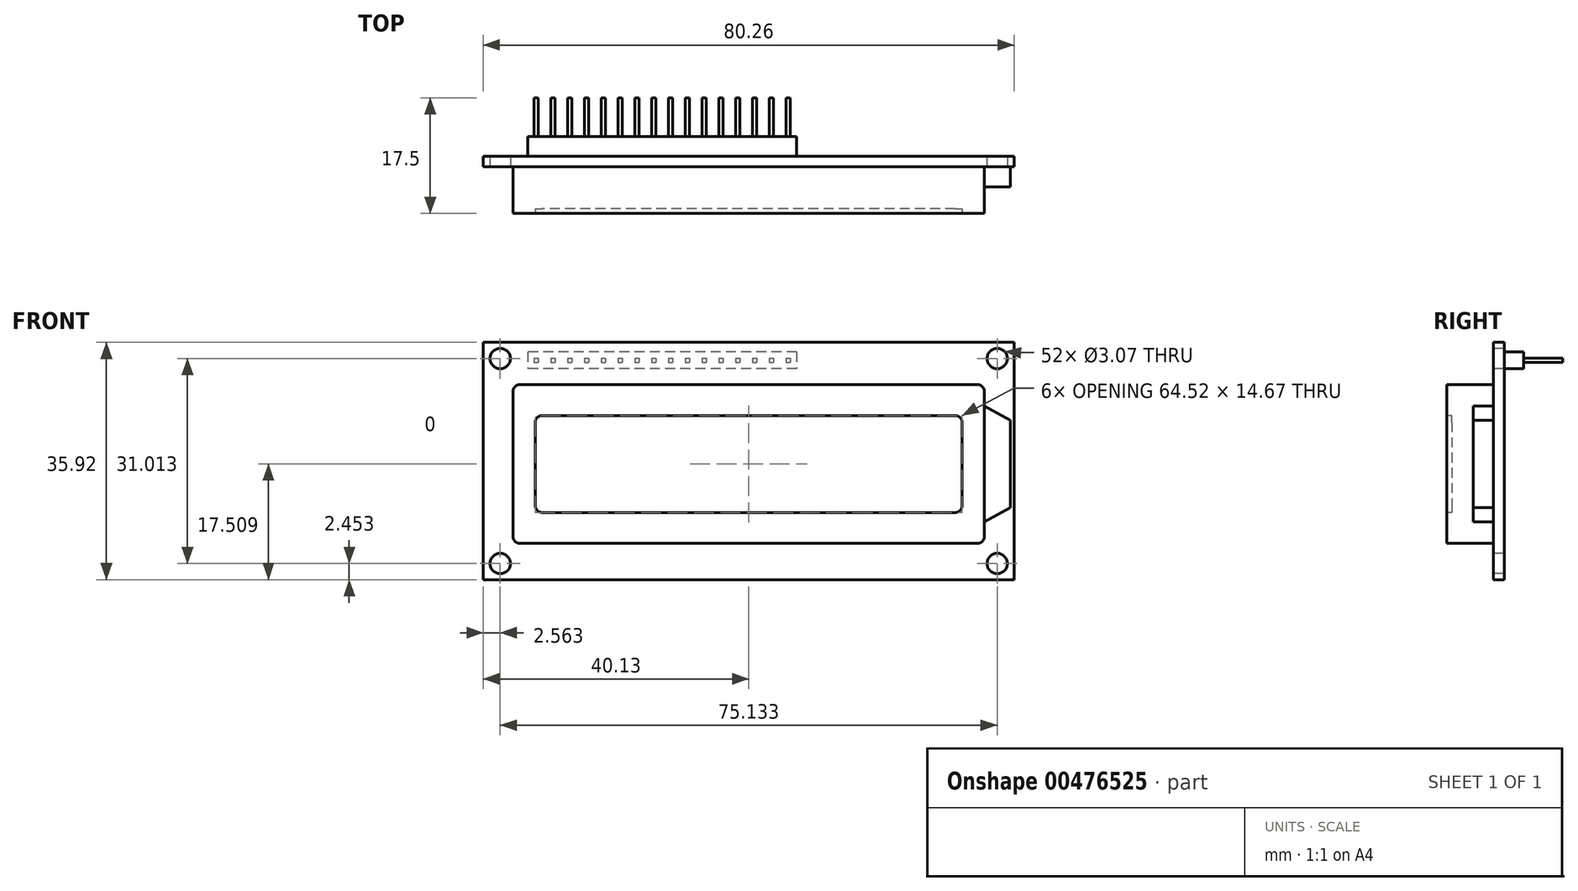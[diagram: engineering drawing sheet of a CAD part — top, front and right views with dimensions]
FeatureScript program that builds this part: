
annotation { "Feature Type Name" : "Feature", "Feature Type Description" : "" }
export const myFeature = defineFeature(function(context is Context, id is Id, definition is map)
    precondition{}
    {
        {
            var Q0;
            Q0=qCreatedBy(makeId("Front.planeOp"),FACE);
            var sketch = newSketch(context, id + "F0", { "sketchPlane" : qUnion([Q0])});
            skLineSegment(sketch, "E0.bottom", {"start": v(40.13, 17.96) * mm, "end": v(-40.13, 17.96) * mm});
            skLineSegment(sketch, "E0.top", {"start": v(40.13, -17.96) * mm, "end": v(-40.13, -17.96) * mm});
            skLineSegment(sketch, "E0.left", {"start": v(40.13, 17.96) * mm, "end": v(40.13, -17.96) * mm});
            skLineSegment(sketch, "E0.right", {"start": v(-40.13, 17.96) * mm, "end": v(-40.13, -17.96) * mm});
            skPoint(sketch, "E0.middle", {"position": v(0, 0) * mm});
            skCircle(sketch, "E1", {"center": v(-37.57, -15.5) * mm, "radius": 1.54 * mm});
            skLineSegment(sketch, "E2", {"start": v(0, 0) * mm, "end": v(0, 12.09) * mm, "construction": true});
            skLineSegment(sketch, "E3", {"start": v(0, 0) * mm, "end": v(12.95, 0) * mm, "construction": true});
            skCircle(sketch, "E4.MirrorC", {"center": v(-37.57, 15.5) * mm, "radius": 1.54 * mm});
            skCircle(sketch, "E5.MirrorC", {"center": v(37.57, -15.5) * mm, "radius": 1.54 * mm});
            skCircle(sketch, "E6.MirrorC", {"center": v(37.57, 15.5) * mm, "radius": 1.54 * mm});
            skSolve(sketch);
        }
        {
            var Q0;
            Q0 = qSketchRegion(id + "F0", true);
            extrude(context, id + "F1", {"entities" : qUnion([Q0]), "oppositeDirection" : true, "depth" : 1.6 * mm});
        }
        {
            var Q0;
            Q0=makeQuery(id+"F1.opExtrude","CAP_FACE",FACE,{"disambiguationData":[OSD([sQuery(id+"F0.wireOp",EDGE,"E0.bottom"),sQuery(id+"F0.wireOp",EDGE,"E0.top"),sQuery(id+"F0.wireOp",EDGE,"E0.left"),sQuery(id+"F0.wireOp",EDGE,"E0.right"),sQuery(id+"F0.wireOp",EDGE,"E4.MirrorC"),sQuery(id+"F0.wireOp",EDGE,"E1"),sQuery(id+"F0.wireOp",EDGE,"E5.MirrorC"),sQuery(id+"F0.wireOp",EDGE,"E6.MirrorC")])],"isStart":true});
            var sketch = newSketch(context, id + "F2", { "sketchPlane" : qUnion([Q0])});
            skLineSegment(sketch, "E7.bottom", {"start": v(-34.6, -12.46) * mm, "end": v(34.6, -12.46) * mm});
            skLineSegment(sketch, "E7.top", {"start": v(-34.6, 11.56) * mm, "end": v(34.6, 11.56) * mm});
            skLineSegment(sketch, "E7.left", {"start": v(-35.62, -11.44) * mm, "end": v(-35.62, 10.54) * mm});
            skLineSegment(sketch, "E7.right", {"start": v(35.62, -11.44) * mm, "end": v(35.62, 10.54) * mm});
            skLineSegment(sketch, "E8", {"start": v(0, 0) * mm, "end": v(0, -12.46) * mm, "construction": true});
            skPoint(sketch, "E8.endSnap0", {"position": v(0, -12.46) * mm});
            skPoint(sketch, "E9.visualSharp", {"position": v(-35.62, 11.56) * mm});
            skArc(sketch, "E9.filletArc", {"start": v(-34.6, 11.56) * mm, "mid": v(-35.33, 11.26) * mm, "end": v(-35.62, 10.54) * mm});
            skPoint(sketch, "E10.visualSharp", {"position": v(-35.62, -12.46) * mm});
            skArc(sketch, "E10.filletArc", {"start": v(-35.62, -11.44) * mm, "mid": v(-35.33, -12.16) * mm, "end": v(-34.6, -12.46) * mm});
            skPoint(sketch, "E11.visualSharp", {"position": v(35.62, -12.46) * mm});
            skArc(sketch, "E11.filletArc", {"start": v(34.6, -12.46) * mm, "mid": v(35.33, -12.16) * mm, "end": v(35.62, -11.44) * mm});
            skPoint(sketch, "E12.visualSharp", {"position": v(35.62, 11.56) * mm});
            skArc(sketch, "E12.filletArc", {"start": v(35.62, 10.54) * mm, "mid": v(35.33, 11.26) * mm, "end": v(34.6, 11.56) * mm});
            skSolve(sketch);
        }
        {
            var Q0;
            Q0=makeQuery(id+"F2.imprint","IMPRINT",FACE,{"disambiguationData":[TD([[makeQuery(id+"F2.imprint","IMPRINT",EDGE,{"derivedFrom":sQuery(id+"F2.wireOp",EDGE,"E7.bottom")}),1.0]])]});
            extrude(context, id + "F3", {"entities" : qUnion([Q0]), "depth" : 7.06 * mm});
        }
        {
            var Q0;
            Q0=makeQuery(id+"F3.opExtrude","CAP_FACE",FACE,{"disambiguationData":[OSD([sQuery(id+"F2.wireOp",EDGE,"E7.bottom"),sQuery(id+"F2.wireOp",EDGE,"E7.top"),sQuery(id+"F2.wireOp",EDGE,"E7.left"),sQuery(id+"F2.wireOp",EDGE,"E7.right"),sQuery(id+"F2.wireOp",EDGE,"E9.filletArc"),sQuery(id+"F2.wireOp",EDGE,"E10.filletArc"),sQuery(id+"F2.wireOp",EDGE,"E11.filletArc"),sQuery(id+"F2.wireOp",EDGE,"E12.filletArc")])],"isStart":false});
            var sketch = newSketch(context, id + "F4", { "sketchPlane" : qUnion([Q0])});
            skLineSegment(sketch, "E13.bottom", {"start": v(31.24, 6.88) * mm, "end": v(-31.24, 6.88) * mm});
            skLineSegment(sketch, "E13.top", {"start": v(31.24, -7.79) * mm, "end": v(-31.24, -7.79) * mm});
            skLineSegment(sketch, "E13.left", {"start": v(32.26, 5.87) * mm, "end": v(32.26, -6.77) * mm});
            skLineSegment(sketch, "E13.right", {"start": v(-32.26, 5.87) * mm, "end": v(-32.26, -6.77) * mm});
            skPoint(sketch, "E13.middle", {"position": v(0, -0.45) * mm});
            skLineSegment(sketch, "E14", {"start": v(-34.6, -11.44) * mm, "end": v(34.6, 10.54) * mm, "construction": true});
            skPoint(sketch, "E15.visualSharp", {"position": v(-32.26, 6.88) * mm});
            skArc(sketch, "E15.filletArc", {"start": v(-31.24, 6.88) * mm, "mid": v(-31.96, 6.59) * mm, "end": v(-32.26, 5.87) * mm});
            skPoint(sketch, "E16.visualSharp", {"position": v(-32.26, -7.79) * mm});
            skArc(sketch, "E16.filletArc", {"start": v(-32.26, -6.77) * mm, "mid": v(-31.96, -7.49) * mm, "end": v(-31.24, -7.79) * mm});
            skPoint(sketch, "E17.visualSharp", {"position": v(32.26, -7.79) * mm});
            skArc(sketch, "E17.filletArc", {"start": v(31.24, -7.79) * mm, "mid": v(31.96, -7.49) * mm, "end": v(32.26, -6.77) * mm});
            skPoint(sketch, "E18.visualSharp", {"position": v(32.26, 6.88) * mm});
            skArc(sketch, "E18.filletArc", {"start": v(32.26, 5.87) * mm, "mid": v(31.96, 6.59) * mm, "end": v(31.24, 6.88) * mm});
            skSolve(sketch);
        }
        {
            var Q0;
            Q0 = qSketchRegion(id + "F4", true);
            extrude(context, id + "F5", {"entities" : qUnion([Q0]), "operationType" : NewBodyOperationType.REMOVE, "oppositeDirection" : true, "depth" : 0.72 * mm});
        }
        {
            var Q0;
            Q0=makeQuery(id+"F1.opExtrude","CAP_FACE",FACE,{"disambiguationData":[OSD([sQuery(id+"F0.wireOp",EDGE,"E0.bottom"),sQuery(id+"F0.wireOp",EDGE,"E0.top"),sQuery(id+"F0.wireOp",EDGE,"E0.left"),sQuery(id+"F0.wireOp",EDGE,"E0.right"),sQuery(id+"F0.wireOp",EDGE,"E4.MirrorC"),sQuery(id+"F0.wireOp",EDGE,"E1"),sQuery(id+"F0.wireOp",EDGE,"E5.MirrorC"),sQuery(id+"F0.wireOp",EDGE,"E6.MirrorC")])],"isStart":true});
            var sketch = newSketch(context, id + "F6", { "sketchPlane" : qUnion([Q0])});
            skLineSegment(sketch, "E19", {"start": v(35.62, 8.31) * mm, "end": v(39.57, 6.15) * mm});
            skLineSegment(sketch, "E20", {"start": v(39.57, 6.15) * mm, "end": v(39.57, -7.05) * mm});
            skLineSegment(sketch, "E21", {"start": v(39.57, -7.05) * mm, "end": v(35.62, -9.21) * mm});
            skLineSegment(sketch, "E22", {"start": v(35.62, 8.31) * mm, "end": v(35.62, -9.21) * mm});
            skLineSegment(sketch, "E23", {"start": v(39.57, -0.45) * mm, "end": v(35.62, -0.45) * mm, "construction": true});
            skSolve(sketch);
        }
        {
            var Q0;
            Q0 = qSketchRegion(id + "F6", true);
            extrude(context, id + "F7", {"entities" : qUnion([Q0]), "depth" : 3.05 * mm});
        }
        {
            var Q0;
            Q0=makeQuery(id+"F1.opExtrude","CAP_FACE",FACE,{"disambiguationData":[OSD([sQuery(id+"F0.wireOp",EDGE,"E0.bottom"),sQuery(id+"F0.wireOp",EDGE,"E0.top"),sQuery(id+"F0.wireOp",EDGE,"E0.left"),sQuery(id+"F0.wireOp",EDGE,"E0.right"),sQuery(id+"F0.wireOp",EDGE,"E4.MirrorC"),sQuery(id+"F0.wireOp",EDGE,"E1"),sQuery(id+"F0.wireOp",EDGE,"E5.MirrorC"),sQuery(id+"F0.wireOp",EDGE,"E6.MirrorC")])],"isStart":false});
            var sketch = newSketch(context, id + "F8", { "sketchPlane" : qUnion([Q0])});
            skLineSegment(sketch, "E24.bottom", {"start": v(-7.25, 16.48) * mm, "end": v(33.39, 16.48) * mm});
            skLineSegment(sketch, "E24.top", {"start": v(-7.25, 13.94) * mm, "end": v(33.39, 13.94) * mm});
            skLineSegment(sketch, "E24.left", {"start": v(-7.25, 16.48) * mm, "end": v(-7.25, 13.94) * mm});
            skLineSegment(sketch, "E24.right", {"start": v(33.39, 16.48) * mm, "end": v(33.39, 13.94) * mm});
            skPoint(sketch, "E25", {"position": v(-7.25, 15.21) * mm});
            skSolve(sketch);
        }
        {
            var Q0;
            Q0 = qSketchRegion(id + "F8", true);
            extrude(context, id + "F9", {"entities" : qUnion([Q0]), "depth" : 2.95 * mm});
        }
        {
            var Q0;
            Q0=makeQuery(id+"F9.opExtrude","CAP_FACE",FACE,{"disambiguationData":[OSD([sQuery(id+"F8.wireOp",EDGE,"E24.bottom"),sQuery(id+"F8.wireOp",EDGE,"E24.top"),sQuery(id+"F8.wireOp",EDGE,"E24.left"),sQuery(id+"F8.wireOp",EDGE,"E24.right")])],"isStart":false});
            var sketch = newSketch(context, id + "F10", { "sketchPlane" : qUnion([Q0])});
            skLineSegment(sketch, "E26.bottom", {"start": v(-5.66, 15.53) * mm, "end": v(-6.3, 15.53) * mm});
            skLineSegment(sketch, "E26.top", {"start": v(-5.66, 14.9) * mm, "end": v(-6.3, 14.9) * mm});
            skLineSegment(sketch, "E26.left", {"start": v(-5.66, 15.53) * mm, "end": v(-5.66, 14.9) * mm});
            skLineSegment(sketch, "E26.right", {"start": v(-6.3, 15.53) * mm, "end": v(-6.3, 14.9) * mm});
            skPoint(sketch, "E26.middle", {"position": v(-5.98, 15.21) * mm});
            skLineSegment(sketch, "E27", {"start": v(-5.98, 15.21) * mm, "end": v(-7.25, 15.21) * mm, "construction": true});
            skLineSegment(sketch, "E28.1.0.0", {"start": v(-3.12, 15.53) * mm, "end": v(-3.76, 15.53) * mm});
            skLineSegment(sketch, "E28.1.0.1", {"start": v(-3.12, 15.53) * mm, "end": v(-3.12, 14.9) * mm});
            skLineSegment(sketch, "E28.1.0.2", {"start": v(-3.12, 14.9) * mm, "end": v(-3.76, 14.9) * mm});
            skLineSegment(sketch, "E28.1.0.3", {"start": v(-3.76, 15.53) * mm, "end": v(-3.76, 14.9) * mm});
            skLineSegment(sketch, "E28.2.0.0", {"start": v(-0.58, 15.53) * mm, "end": v(-1.22, 15.53) * mm});
            skLineSegment(sketch, "E28.2.0.1", {"start": v(-0.58, 15.53) * mm, "end": v(-0.58, 14.9) * mm});
            skLineSegment(sketch, "E28.2.0.2", {"start": v(-0.58, 14.9) * mm, "end": v(-1.22, 14.9) * mm});
            skLineSegment(sketch, "E28.2.0.3", {"start": v(-1.22, 15.53) * mm, "end": v(-1.22, 14.9) * mm});
            skLineSegment(sketch, "E28.3.0.0", {"start": v(1.96, 15.53) * mm, "end": v(1.32, 15.53) * mm});
            skLineSegment(sketch, "E28.3.0.1", {"start": v(1.96, 15.53) * mm, "end": v(1.96, 14.9) * mm});
            skLineSegment(sketch, "E28.3.0.2", {"start": v(1.96, 14.9) * mm, "end": v(1.32, 14.9) * mm});
            skLineSegment(sketch, "E28.3.0.3", {"start": v(1.32, 15.53) * mm, "end": v(1.32, 14.9) * mm});
            skLineSegment(sketch, "E28.4.0.0", {"start": v(4.5, 15.53) * mm, "end": v(3.86, 15.53) * mm});
            skLineSegment(sketch, "E28.4.0.1", {"start": v(4.5, 15.53) * mm, "end": v(4.5, 14.9) * mm});
            skLineSegment(sketch, "E28.4.0.2", {"start": v(4.5, 14.9) * mm, "end": v(3.86, 14.9) * mm});
            skLineSegment(sketch, "E28.4.0.3", {"start": v(3.86, 15.53) * mm, "end": v(3.86, 14.9) * mm});
            skLineSegment(sketch, "E28.5.0.0", {"start": v(7.04, 15.53) * mm, "end": v(6.4, 15.53) * mm});
            skLineSegment(sketch, "E28.5.0.1", {"start": v(7.04, 15.53) * mm, "end": v(7.04, 14.9) * mm});
            skLineSegment(sketch, "E28.5.0.2", {"start": v(7.04, 14.9) * mm, "end": v(6.4, 14.9) * mm});
            skLineSegment(sketch, "E28.5.0.3", {"start": v(6.4, 15.53) * mm, "end": v(6.4, 14.9) * mm});
            skLineSegment(sketch, "E28.6.0.0", {"start": v(9.58, 15.53) * mm, "end": v(8.94, 15.53) * mm});
            skLineSegment(sketch, "E28.6.0.1", {"start": v(9.58, 15.53) * mm, "end": v(9.58, 14.9) * mm});
            skLineSegment(sketch, "E28.6.0.2", {"start": v(9.58, 14.9) * mm, "end": v(8.94, 14.9) * mm});
            skLineSegment(sketch, "E28.6.0.3", {"start": v(8.94, 15.53) * mm, "end": v(8.94, 14.9) * mm});
            skLineSegment(sketch, "E28.7.0.0", {"start": v(12.12, 15.53) * mm, "end": v(11.48, 15.53) * mm});
            skLineSegment(sketch, "E28.7.0.1", {"start": v(12.12, 15.53) * mm, "end": v(12.12, 14.9) * mm});
            skLineSegment(sketch, "E28.7.0.2", {"start": v(12.12, 14.9) * mm, "end": v(11.48, 14.9) * mm});
            skLineSegment(sketch, "E28.7.0.3", {"start": v(11.48, 15.53) * mm, "end": v(11.48, 14.9) * mm});
            skLineSegment(sketch, "E28.8.0.0", {"start": v(14.66, 15.53) * mm, "end": v(14.02, 15.53) * mm});
            skLineSegment(sketch, "E28.8.0.1", {"start": v(14.66, 15.53) * mm, "end": v(14.66, 14.9) * mm});
            skLineSegment(sketch, "E28.8.0.2", {"start": v(14.66, 14.9) * mm, "end": v(14.02, 14.9) * mm});
            skLineSegment(sketch, "E28.8.0.3", {"start": v(14.02, 15.53) * mm, "end": v(14.02, 14.9) * mm});
            skLineSegment(sketch, "E28.9.0.0", {"start": v(17.2, 15.53) * mm, "end": v(16.56, 15.53) * mm});
            skLineSegment(sketch, "E28.9.0.1", {"start": v(17.2, 15.53) * mm, "end": v(17.2, 14.9) * mm});
            skLineSegment(sketch, "E28.9.0.2", {"start": v(17.2, 14.9) * mm, "end": v(16.56, 14.9) * mm});
            skLineSegment(sketch, "E28.9.0.3", {"start": v(16.56, 15.53) * mm, "end": v(16.56, 14.9) * mm});
            skLineSegment(sketch, "E28.10.0.0", {"start": v(19.74, 15.53) * mm, "end": v(19.1, 15.53) * mm});
            skLineSegment(sketch, "E28.10.0.1", {"start": v(19.74, 15.53) * mm, "end": v(19.74, 14.9) * mm});
            skLineSegment(sketch, "E28.10.0.2", {"start": v(19.74, 14.9) * mm, "end": v(19.1, 14.9) * mm});
            skLineSegment(sketch, "E28.10.0.3", {"start": v(19.1, 15.53) * mm, "end": v(19.1, 14.9) * mm});
            skLineSegment(sketch, "E28.11.0.0", {"start": v(22.28, 15.53) * mm, "end": v(21.64, 15.53) * mm});
            skLineSegment(sketch, "E28.11.0.1", {"start": v(22.28, 15.53) * mm, "end": v(22.28, 14.9) * mm});
            skLineSegment(sketch, "E28.11.0.2", {"start": v(22.28, 14.9) * mm, "end": v(21.64, 14.9) * mm});
            skLineSegment(sketch, "E28.11.0.3", {"start": v(21.64, 15.53) * mm, "end": v(21.64, 14.9) * mm});
            skLineSegment(sketch, "E28.12.0.0", {"start": v(24.82, 15.53) * mm, "end": v(24.18, 15.53) * mm});
            skLineSegment(sketch, "E28.12.0.1", {"start": v(24.82, 15.53) * mm, "end": v(24.82, 14.9) * mm});
            skLineSegment(sketch, "E28.12.0.2", {"start": v(24.82, 14.9) * mm, "end": v(24.18, 14.9) * mm});
            skLineSegment(sketch, "E28.12.0.3", {"start": v(24.18, 15.53) * mm, "end": v(24.18, 14.9) * mm});
            skLineSegment(sketch, "E28.13.0.0", {"start": v(27.36, 15.53) * mm, "end": v(26.72, 15.53) * mm});
            skLineSegment(sketch, "E28.13.0.1", {"start": v(27.36, 15.53) * mm, "end": v(27.36, 14.9) * mm});
            skLineSegment(sketch, "E28.13.0.2", {"start": v(27.36, 14.9) * mm, "end": v(26.72, 14.9) * mm});
            skLineSegment(sketch, "E28.13.0.3", {"start": v(26.72, 15.53) * mm, "end": v(26.72, 14.9) * mm});
            skLineSegment(sketch, "E28.14.0.0", {"start": v(29.9, 15.53) * mm, "end": v(29.26, 15.53) * mm});
            skLineSegment(sketch, "E28.14.0.1", {"start": v(29.9, 15.53) * mm, "end": v(29.9, 14.9) * mm});
            skLineSegment(sketch, "E28.14.0.2", {"start": v(29.9, 14.9) * mm, "end": v(29.26, 14.9) * mm});
            skLineSegment(sketch, "E28.14.0.3", {"start": v(29.26, 15.53) * mm, "end": v(29.26, 14.9) * mm});
            skLineSegment(sketch, "E28.15.0.0", {"start": v(32.44, 15.53) * mm, "end": v(31.8, 15.53) * mm});
            skLineSegment(sketch, "E28.15.0.1", {"start": v(32.44, 15.53) * mm, "end": v(32.44, 14.9) * mm});
            skLineSegment(sketch, "E28.15.0.2", {"start": v(32.44, 14.9) * mm, "end": v(31.8, 14.9) * mm});
            skLineSegment(sketch, "E28.15.0.3", {"start": v(31.8, 15.53) * mm, "end": v(31.8, 14.9) * mm});
            skLineSegment(sketch, "E28.direction1", {"start": v(-6.3, 14.9) * mm, "end": v(-3.76, 14.9) * mm, "construction": true});
            skLineSegment(sketch, "E29", {"start": v(13.07, 13.94) * mm, "end": v(13.07, 13.95) * mm, "construction": true});
            skPoint(sketch, "E29.endSnap0", {"position": v(13.07, 16.48) * mm});
            skSolve(sketch);
        }
        {
            var Q0;
            Q0 = qSketchRegion(id + "F10", true);
            extrude(context, id + "F11", {"entities" : qUnion([Q0]), "depth" : 5.9 * mm});
        }
    });
